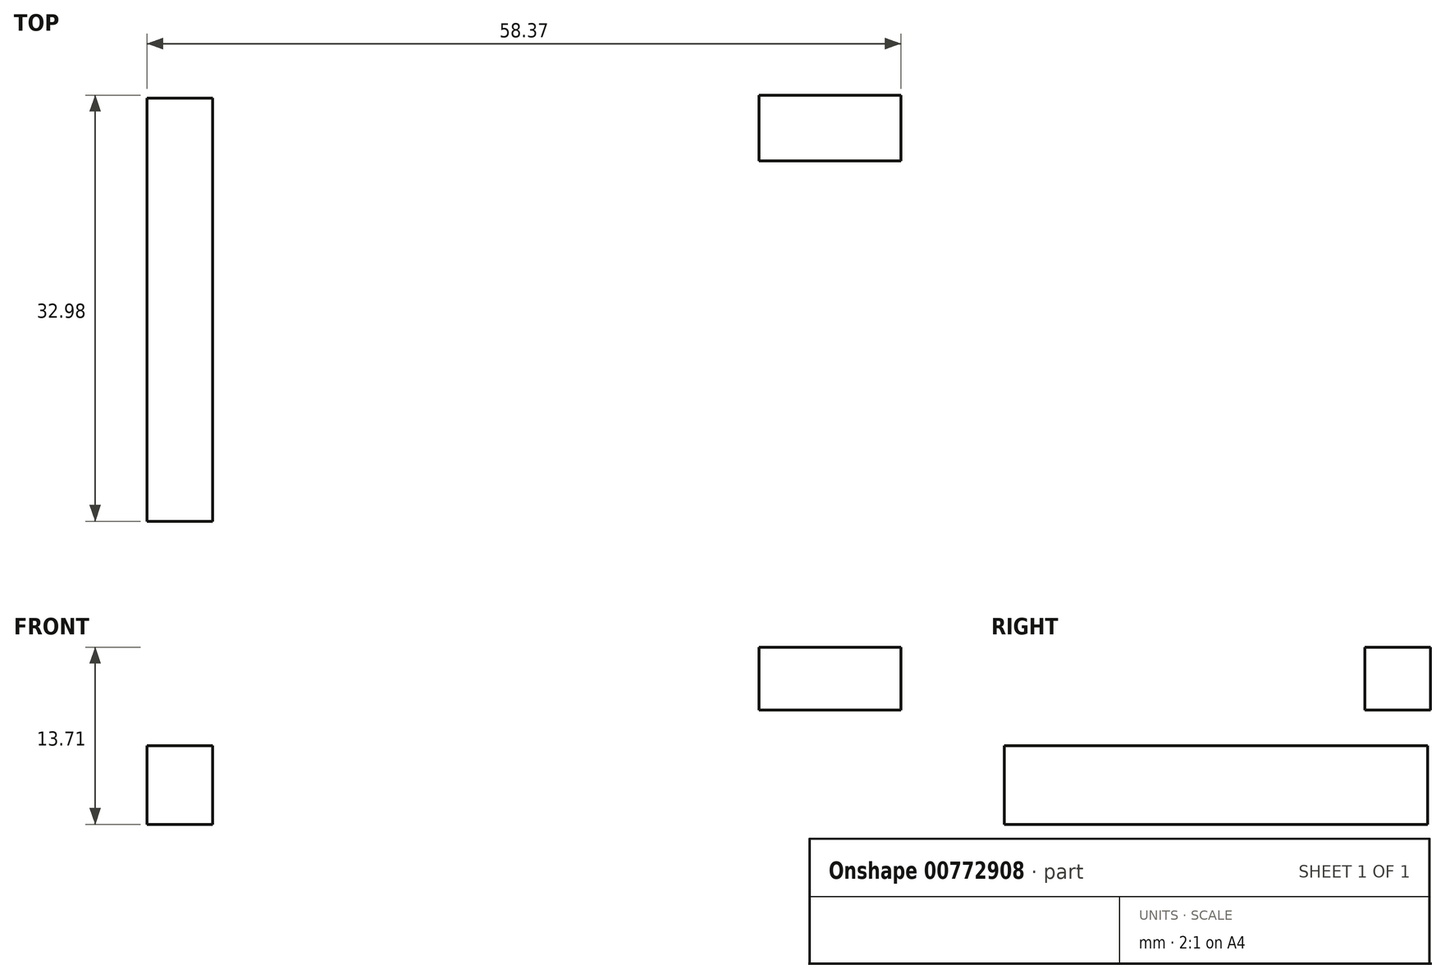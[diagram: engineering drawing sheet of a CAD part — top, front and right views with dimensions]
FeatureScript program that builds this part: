
annotation { "Feature Type Name" : "Feature", "Feature Type Description" : "" }
export const myFeature = defineFeature(function(context is Context, id is Id, definition is map)
    precondition{}
    {
        {
            var Q0;
            Q0=qCreatedBy(makeId("Right.planeOp"),FACE);
            var sketch = newSketch(context, id + "F0", { "sketchPlane" : qUnion([Q0])});
            skLineSegment(sketch, "E0.bottom", {"start": v(-32.98, 14.94) * mm, "end": v(-0.22, 14.94) * mm});
            skLineSegment(sketch, "E0.top", {"start": v(-32.98, 21.03) * mm, "end": v(-0.22, 21.03) * mm});
            skLineSegment(sketch, "E0.left", {"start": v(-32.98, 14.94) * mm, "end": v(-32.98, 21.03) * mm});
            skLineSegment(sketch, "E0.right", {"start": v(-0.22, 14.94) * mm, "end": v(-0.22, 21.03) * mm});
            skPoint(sketch, "E0.middle", {"position": v(-16.6, 17.98) * mm});
            skSolve(sketch);
        }
        {
            var Q0;
            Q0 = qSketchRegion(id + "F0", true);
            extrude(context, id + "F1", {"entities" : qUnion([Q0]), "depth" : 5.08 * mm, "offsetDistance" : 25.4 * mm});
        }
        {
            var Q0;
            Q0=qCreatedBy(makeId("Front.planeOp"),FACE);
            var sketch = newSketch(context, id + "F2", { "sketchPlane" : qUnion([Q0])});
            skLineSegment(sketch, "E1.bottom", {"start": v(58.37, 23.77) * mm, "end": v(47.4, 23.77) * mm});
            skLineSegment(sketch, "E1.top", {"start": v(58.37, 28.65) * mm, "end": v(47.4, 28.65) * mm});
            skLineSegment(sketch, "E1.left", {"start": v(58.37, 23.77) * mm, "end": v(58.37, 28.65) * mm});
            skLineSegment(sketch, "E1.right", {"start": v(47.4, 23.77) * mm, "end": v(47.4, 28.65) * mm});
            skPoint(sketch, "E1.middle", {"position": v(52.88, 26.21) * mm});
            skSolve(sketch);
        }
        {
            var Q0;
            Q0 = qSketchRegion(id + "F2", true);
            extrude(context, id + "F3", {"entities" : qUnion([Q0]), "depth" : 5.08 * mm, "offsetDistance" : 25.4 * mm});
        }
    });
